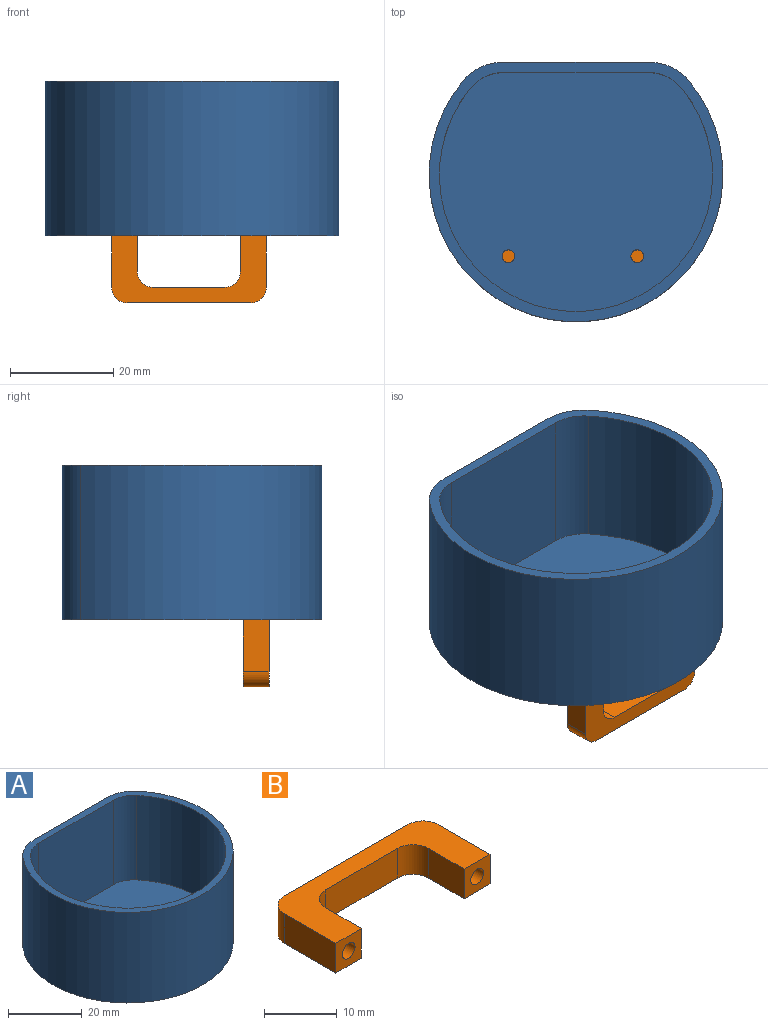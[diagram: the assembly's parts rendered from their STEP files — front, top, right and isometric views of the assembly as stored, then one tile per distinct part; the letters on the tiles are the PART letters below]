
ASSEMBLY  parts=2 mates=1
PART A: 101 faces, bbox 57x50.3x30 mm
  f0: plane 57x50.34mm, normal (0,0,-1), area 2244.8mm2, adj f1,f2,f3,f4,f18,f19,f20,f21
  f1: plane 30x28.43mm, normal (0,1,0), area 852.8mm2, adj f0,f2,f4,f5
  f2: cylinder r=10mm len=30mm, axis (0,0,-1), area 262.9mm2, adj f0,f1,f3,f5
  f3: cylinder r=28.5mm len=57mm, axis (0,0,-1), area 3873.8mm2, adj f0,f2,f4,f5
  f4: cylinder r=10mm len=30mm, axis (0,0,-1), area 262.9mm2, adj f0,f1,f3,f5
  f5: plane 57x50.34mm, normal (0,0,1), area 337.6mm2, adj f1,f2,f3,f4,f6,f7,f8,f9
  f6: plane 28.43x28mm, normal (0,-1,0), area 796mm2, adj f5,f7,f9,f10
  f7: cylinder r=8mm len=28mm, axis (0,0,-1), area 196.3mm2, adj f5,f6,f8,f10
  f8: cylinder r=26.5mm len=53mm, axis (0,0,-1), area 3361.8mm2, adj f5,f7,f9,f10
  f9: cylinder r=8mm len=28mm, axis (0,0,-1), area 196.3mm2, adj f5,f6,f8,f10
  f10: plane 53x46.34mm, normal (0,0,1), area 2032.9mm2, adj f6,f7,f8,f9,f99,f100
  f11: extruded ~2.17x1mm, area 2.3mm2, adj f12,f27,f28,f98
  f12: extruded ~2.16x1mm, area 2.3mm2, adj f11,f13,f28,f98
  f13: extruded ~1.67x1mm, area 1.9mm2, adj f12,f14,f28,f98
  f14: extruded ~1.69x1mm, area 1.9mm2, adj f13,f15,f28,f98
  f15: extruded ~2.15x1mm, area 2.3mm2, adj f14,f16,f28,f98
  f16: extruded ~2.17x1mm, area 2.3mm2, adj f15,f17,f28,f98
  f17: extruded ~1.68x1mm, area 1.9mm2, adj f16,f27,f28,f98
  f18: extruded ~2.84x1mm, area 3.1mm2, adj f0,f19,f26,f28
  f19: extruded ~2.81x1mm, area 3mm2, adj f0,f18,f20,f28
  f20: extruded ~2.48x1.04mm, area 2.8mm2, adj f0,f19,f21,f28
  f21: extruded ~2.52x1.01mm, area 2.8mm2, adj f0,f20,f22,f28
  f22: extruded ~2.83x1mm, area 3mm2, adj f0,f21,f23,f28
  f23: extruded ~2.05x1mm, area 2.1mm2, adj f0,f22,f24,f28
  f24: extruded ~1.34x1.19mm, area 1.8mm2, adj f0,f23,f25,f28
  f25: extruded ~1.77x1mm, area 1.9mm2, adj f0,f24,f26,f28
  f26: extruded ~2.53x1.02mm, area 2.8mm2, adj f0,f18,f25,f28
  f27: extruded ~1.67x1mm, area 1.9mm2, adj f11,f17,f28,f98
  f28: plane 7.71x6.83mm, normal (0,0,-1), area 21.2mm2, adj f11,f12,f13,f14,f15,f16,f17,f18
  f29: plane 4.84x1mm, normal (-1,0,0), area 4.8mm2, adj f0,f30,f56,f57
  f30: plane 1.12x1mm, normal (0,1,0), area 1.1mm2, adj f0,f29,f31,f57
  f31: plane 4.85x1mm, normal (1,0,0), area 4.8mm2, adj f0,f30,f32,f57
  f32: extruded ~2.07x1mm, area 2.2mm2, adj f0,f31,f33,f57
  f33: extruded ~1.89x1mm, area 2.1mm2, adj f0,f32,f34,f57
  f34: extruded ~1.44x1mm, area 1.5mm2, adj f0,f33,f35,f57
  f35: extruded ~1x0.96mm, area 1.4mm2, adj f0,f34,f36,f57
  f36: plane 1x0.05mm, normal (0,-1,0), area 0.1mm2, adj f0,f35,f37,f57
  f37: extruded ~2.28x1.26mm, area 2.8mm2, adj f0,f36,f38,f57
  f38: extruded ~1.3x1mm, area 1.3mm2, adj f0,f37,f39,f57
  f39: extruded ~1x0.9mm, area 1.3mm2, adj f0,f38,f40,f57
  f40: plane 1x0.05mm, normal (0,-1,0), area 0.1mm2, adj f0,f39,f41,f57
  f41: plane 1.02x1mm, normal (0.98,-0.18,0), area 1mm2, adj f0,f40,f42,f57
  f42: plane 1x0.92mm, normal (0,-1,0), area 0.9mm2, adj f0,f41,f43,f57
  f43: plane 7.43x1mm, normal (-1,0,0), area 7.4mm2, adj f0,f42,f44,f57
  f44: plane 1.13x1mm, normal (0,1,0), area 1.1mm2, adj f0,f43,f45,f57
  f45: plane 3.9x1mm, normal (1,0,0), area 3.9mm2, adj f0,f44,f46,f57
  f46: extruded ~2.08x1mm, area 2.2mm2, adj f0,f45,f47,f57
  f47: extruded ~1.55x1mm, area 1.7mm2, adj f0,f46,f48,f57
  f48: extruded ~1.19x1mm, area 1.3mm2, adj f0,f47,f49,f57
  f49: extruded ~1.33x1mm, area 1.4mm2, adj f0,f48,f50,f57
  f50: plane 4.84x1mm, normal (-1,0,0), area 4.8mm2, adj f0,f49,f51,f57
  f51: plane 1.13x1mm, normal (0,1,0), area 1.1mm2, adj f0,f50,f52,f57
  f52: plane 4.15x1mm, normal (1,0,0), area 4.2mm2, adj f0,f51,f53,f57
  f53: extruded ~1.86x1mm, area 2mm2, adj f0,f52,f54,f57
  f54: extruded ~1.55x1mm, area 1.7mm2, adj f0,f53,f55,f57
  f55: extruded ~1.18x1mm, area 1.3mm2, adj f0,f54,f56,f57
  f56: extruded ~1.33x1mm, area 1.4mm2, adj f0,f29,f55,f57
  f57: plane 10.6x7.57mm, normal (0,0,-1), area 31.3mm2, adj f29,f30,f31,f32,f33,f34,f35,f36
  f58: plane 4.84x1mm, normal (-1,0,0), area 4.8mm2, adj f0,f59,f85,f86
  f59: plane 1.12x1mm, normal (0,1,0), area 1.1mm2, adj f0,f58,f60,f86
  f60: plane 4.85x1mm, normal (1,0,0), area 4.8mm2, adj f0,f59,f61,f86
  f61: extruded ~2.07x1mm, area 2.2mm2, adj f0,f60,f62,f86
  f62: extruded ~1.89x1mm, area 2.1mm2, adj f0,f61,f63,f86
  f63: extruded ~1.44x1mm, area 1.5mm2, adj f0,f62,f64,f86
  f64: extruded ~1x0.96mm, area 1.4mm2, adj f0,f63,f65,f86
  f65: plane 1x0.05mm, normal (0,-1,0), area 0.1mm2, adj f0,f64,f66,f86
  f66: extruded ~2.28x1.26mm, area 2.8mm2, adj f0,f65,f67,f86
  f67: extruded ~1.3x1mm, area 1.3mm2, adj f0,f66,f68,f86
  f68: extruded ~1x0.9mm, area 1.3mm2, adj f0,f67,f69,f86
  f69: plane 1x0.05mm, normal (0,-1,0), area 0.1mm2, adj f0,f68,f70,f86
  f70: plane 1.02x1mm, normal (0.98,-0.18,0), area 1mm2, adj f0,f69,f71,f86
  f71: plane 1x0.92mm, normal (0,-1,0), area 0.9mm2, adj f0,f70,f72,f86
  f72: plane 7.43x1mm, normal (-1,0,0), area 7.4mm2, adj f0,f71,f73,f86
  f73: plane 1.13x1mm, normal (0,1,0), area 1.1mm2, adj f0,f72,f74,f86
  f74: plane 3.9x1mm, normal (1,0,0), area 3.9mm2, adj f0,f73,f75,f86
  f75: extruded ~2.08x1mm, area 2.2mm2, adj f0,f74,f76,f86
  f76: extruded ~1.55x1mm, area 1.7mm2, adj f0,f75,f77,f86
  f77: extruded ~1.19x1mm, area 1.3mm2, adj f0,f76,f78,f86
  f78: extruded ~1.33x1mm, area 1.4mm2, adj f0,f77,f79,f86
  f79: plane 4.84x1mm, normal (-1,0,0), area 4.8mm2, adj f0,f78,f80,f86
  f80: plane 1.13x1mm, normal (0,1,0), area 1.1mm2, adj f0,f79,f81,f86
  f81: plane 4.15x1mm, normal (1,0,0), area 4.2mm2, adj f0,f80,f82,f86
  f82: extruded ~1.86x1mm, area 2mm2, adj f0,f81,f83,f86
  f83: extruded ~1.55x1mm, area 1.7mm2, adj f0,f82,f84,f86
  f84: extruded ~1.18x1mm, area 1.3mm2, adj f0,f83,f85,f86
  f85: extruded ~1.33x1mm, area 1.4mm2, adj f0,f58,f84,f86
  f86: plane 10.6x7.57mm, normal (0,0,-1), area 31.3mm2, adj f58,f59,f60,f61,f62,f63,f64,f65
  f87: plane 1.15x1mm, normal (0,1,0), area 1.2mm2, adj f0,f88,f96,f97
  f88: plane 4.24x1mm, normal (1,0,0), area 4.2mm2, adj f0,f87,f89,f97
  f89: plane 4.11x1mm, normal (0,1,0), area 4.1mm2, adj f0,f88,f90,f97
  f90: plane 1.02x1mm, normal (1,0,0), area 1mm2, adj f0,f89,f91,f97
  f91: plane 4.11x1mm, normal (0,-1,0), area 4.1mm2, adj f0,f90,f92,f97
  f92: plane 3.63x1mm, normal (1,0,0), area 3.6mm2, adj f0,f91,f93,f97
  f93: plane 4.38x1mm, normal (0,1,0), area 4.4mm2, adj f0,f92,f94,f97
  f94: plane 1.02x1mm, normal (1,0,0), area 1mm2, adj f0,f93,f95,f97
  f95: plane 5.53x1mm, normal (0,-1,0), area 5.5mm2, adj f0,f94,f96,f97
  f96: plane 9.92x1mm, normal (-1,0,0), area 9.9mm2, adj f0,f87,f95,f97
  f97: plane 9.92x5.53mm, normal (0,0,-1), area 20.1mm2, adj f87,f88,f89,f90,f91,f92,f93,f94
  f98: plane 5.81x4.5mm, normal (0,0,-1), area 21.7mm2, adj f11,f12,f13,f14,f15,f16,f17,f27
  f99: cylinder r=1.25mm len=2.5mm, axis (0,0,-1), area 15.7mm2, adj f0,f10
  f100: cylinder r=1.25mm len=2.5mm, axis (0,0,-1), area 15.7mm2, adj f0,f10
PART B: 18 faces, bbox 30x13x5 mm
  f0: plane 10x5mm, normal (1,0,0), area 50mm2, adj f7,f8,f9,f14
  f1: plane 24x5mm, normal (0,1,0), area 120mm2, adj f8,f9,f14,f15
  f2: plane 10x5mm, normal (-1,0,0), area 50mm2, adj f3,f8,f9,f15
  f3: plane 5x5mm, normal (0,-1,0), area 20.1mm2, adj f2,f4,f8,f9,f12
  f4: plane 7x5mm, normal (1,0,0), area 35mm2, adj f3,f8,f9,f16
  f5: plane 14x5mm, normal (0,-1,0), area 70mm2, adj f8,f9,f16,f17
  f6: plane 7x5mm, normal (-1,0,0), area 35mm2, adj f7,f8,f9,f17
  f7: plane 5x5mm, normal (0,-1,0), area 20.1mm2, adj f0,f6,f8,f9,f10
  f8: plane 30x13mm, normal (0,0,1), area 190mm2, adj f0,f1,f2,f3,f4,f5,f6,f7
  f9: plane 30x13mm, normal (0,0,-1), area 190mm2, adj f0,f1,f2,f3,f4,f5,f6,f7
  f10: cylinder r=1.25mm len=12mm, axis (0,-1,0), area 94.2mm2, adj f7,f11
  f11: plane 2.5x2.5mm, normal (0,-1,0), area 4.9mm2, adj f10
  f12: cylinder r=1.25mm len=12mm, axis (0,-1,0), area 94.2mm2, adj f3,f13
  f13: plane 2.5x2.5mm, normal (0,-1,0), area 4.9mm2, adj f12
  f14: cylinder r=3mm len=5mm, axis (0,0,1), area 23.6mm2, adj f0,f1,f8,f9
  f15: cylinder r=3mm len=5mm, axis (0,0,-1), area 23.6mm2, adj f1,f2,f8,f9
  f16: cylinder r=3mm len=5mm, axis (0,0,1), area 23.6mm2, adj f4,f5,f8,f9
  f17: cylinder r=3mm len=5mm, axis (0,0,1), area 23.6mm2, adj f5,f6,f8,f9
PLACE A t=(6.1,-39.34,14.77)mm
PLACE B rot(axis=(-1,0,0),90deg) t=(-4.51,-57.58,43.8)mm
MATE fastened B.f10 <-> A.f99  axis (0,0,1) through (17.99,-55.08,14.77)mm
